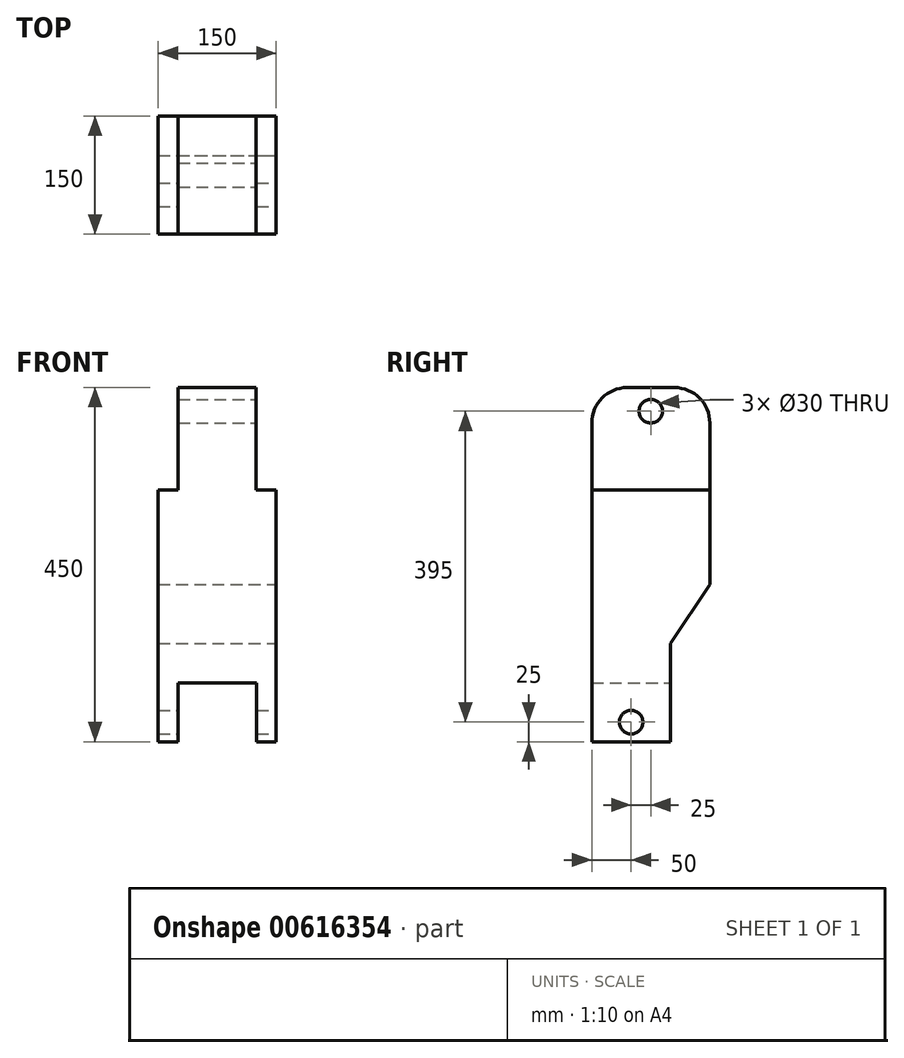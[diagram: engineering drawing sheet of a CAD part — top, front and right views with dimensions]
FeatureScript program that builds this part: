
annotation { "Feature Type Name" : "Feature", "Feature Type Description" : "" }
export const myFeature = defineFeature(function(context is Context, id is Id, definition is map)
    precondition{}
    {
        {
            var Q0;
            Q0=qCreatedBy(makeId("Front.planeOp"),FACE);
            var sketch = newSketch(context, id + "F0", { "sketchPlane" : qUnion([Q0])});
            skLineSegment(sketch, "E0", {"start": v(0, 0) * mm, "end": v(-50, 0) * mm});
            skLineSegment(sketch, "E1", {"start": v(-50, 0) * mm, "end": v(-50, -75) * mm});
            skLineSegment(sketch, "E2", {"start": v(-50, -75) * mm, "end": v(-75, -75) * mm});
            skLineSegment(sketch, "E3", {"start": v(-75, -75) * mm, "end": v(-75, 245) * mm});
            skLineSegment(sketch, "E4", {"start": v(-75, 245) * mm, "end": v(-49.5, 245) * mm});
            skLineSegment(sketch, "E5", {"start": v(-49.5, 245) * mm, "end": v(-49.5, 375) * mm});
            skLineSegment(sketch, "E6", {"start": v(-49.5, 375) * mm, "end": v(49.5, 375) * mm});
            skLineSegment(sketch, "E7.MirrorCS", {"start": v(49.5, 245) * mm, "end": v(49.5, 375) * mm});
            skLineSegment(sketch, "E8.MirrorCS", {"start": v(75, 245) * mm, "end": v(49.5, 245) * mm});
            skLineSegment(sketch, "E9.MirrorCS", {"start": v(75, -75) * mm, "end": v(75, 245) * mm});
            skLineSegment(sketch, "E10.MirrorCS", {"start": v(50, -75) * mm, "end": v(75, -75) * mm});
            skLineSegment(sketch, "E11.MirrorCS", {"start": v(50, 0) * mm, "end": v(50, -75) * mm});
            skLineSegment(sketch, "E12.MirrorCS", {"start": v(0, 0) * mm, "end": v(50, 0) * mm});
            skSolve(sketch);
        }
        {
            var Q0;
            Q0 = qSketchRegion(id + "F0", true);
            extrude(context, id + "F1", {"entities" : qUnion([Q0]), "depth" : 150 * mm, "offsetDistance" : 25 * mm});
        }
        {
            var Q0;
            Q0=makeQuery(id+"F1.opExtrude","SWEPT_FACE",FACE,{"disambiguationData":[OSD([sQuery(id+"F0.wireOp",EDGE,"E9.MirrorCS")])]});
            var sketch = newSketch(context, id + "F2", { "sketchPlane" : qUnion([Q0])});
            skLineSegment(sketch, "E13", {"start": v(-50, -75) * mm, "end": v(-50, 50) * mm});
            skLineSegment(sketch, "E14", {"start": v(-50, 50) * mm, "end": v(0, 125) * mm});
            skLineSegment(sketch, "E15", {"start": v(-50, -75) * mm, "end": v(0, -75) * mm});
            skLineSegment(sketch, "E16", {"start": v(0, -75) * mm, "end": v(0, 125) * mm});
            skSolve(sketch);
        }
        {
            var Q0;
            Q0 = qSketchRegion(id + "F2", true);
            extrude(context, id + "F3", {"entities" : qUnion([Q0]), "operationType" : NewBodyOperationType.REMOVE, "oppositeDirection" : true, "depth" : 188 * mm, "offsetDistance" : 25 * mm});
        }
        {
            var Q0;
            Q0=makeQuery(id+"F1.opExtrude","CAP_EDGE",EDGE,{"disambiguationData":[OSD([sQuery(id+"F0.wireOp",EDGE,"E6")])],"isStart":false});
            var Q1;
            Q1=makeQuery(id+"F1.opExtrude","CAP_EDGE",EDGE,{"disambiguationData":[OSD([sQuery(id+"F0.wireOp",EDGE,"E6")])],"isStart":true});
            fillet(context, id + "F4", {"entities" : qUnion([Q0, Q1]), "radius" : 45 * mm, "tangentPropagation" : true, "allowEdgeOverflow" : false});
        }
        {
            var Q0;
            Q0=makeQuery(id+"F1.opExtrude","SWEPT_FACE",FACE,{"disambiguationData":[OSD([sQuery(id+"F0.wireOp",EDGE,"E7.MirrorCS")])]});
            var sketch = newSketch(context, id + "F5", { "sketchPlane" : qUnion([Q0])});
            skCircle(sketch, "E17", {"center": v(-75, 345) * mm, "radius": 15 * mm});
            skSolve(sketch);
        }
        {
            var Q0;
            Q0 = qSketchRegion(id + "F5", true);
            extrude(context, id + "F6", {"entities" : qUnion([Q0]), "operationType" : NewBodyOperationType.REMOVE, "oppositeDirection" : true, "depth" : 133 * mm, "offsetDistance" : 25 * mm});
        }
        {
            var Q0;
            Q0=makeQuery(id+"F1.opExtrude","SWEPT_FACE",FACE,{"disambiguationData":[OSD([sQuery(id+"F0.wireOp",EDGE,"E9.MirrorCS")])]});
            var sketch = newSketch(context, id + "F7", { "sketchPlane" : qUnion([Q0])});
            skCircle(sketch, "E18", {"center": v(-100, -50) * mm, "radius": 15 * mm});
            skSolve(sketch);
        }
        {
            var Q0;
            Q0 = qSketchRegion(id + "F7", true);
            extrude(context, id + "F8", {"entities" : qUnion([Q0]), "operationType" : NewBodyOperationType.REMOVE, "oppositeDirection" : true, "depth" : 179 * mm, "offsetDistance" : 25 * mm});
        }
    });
